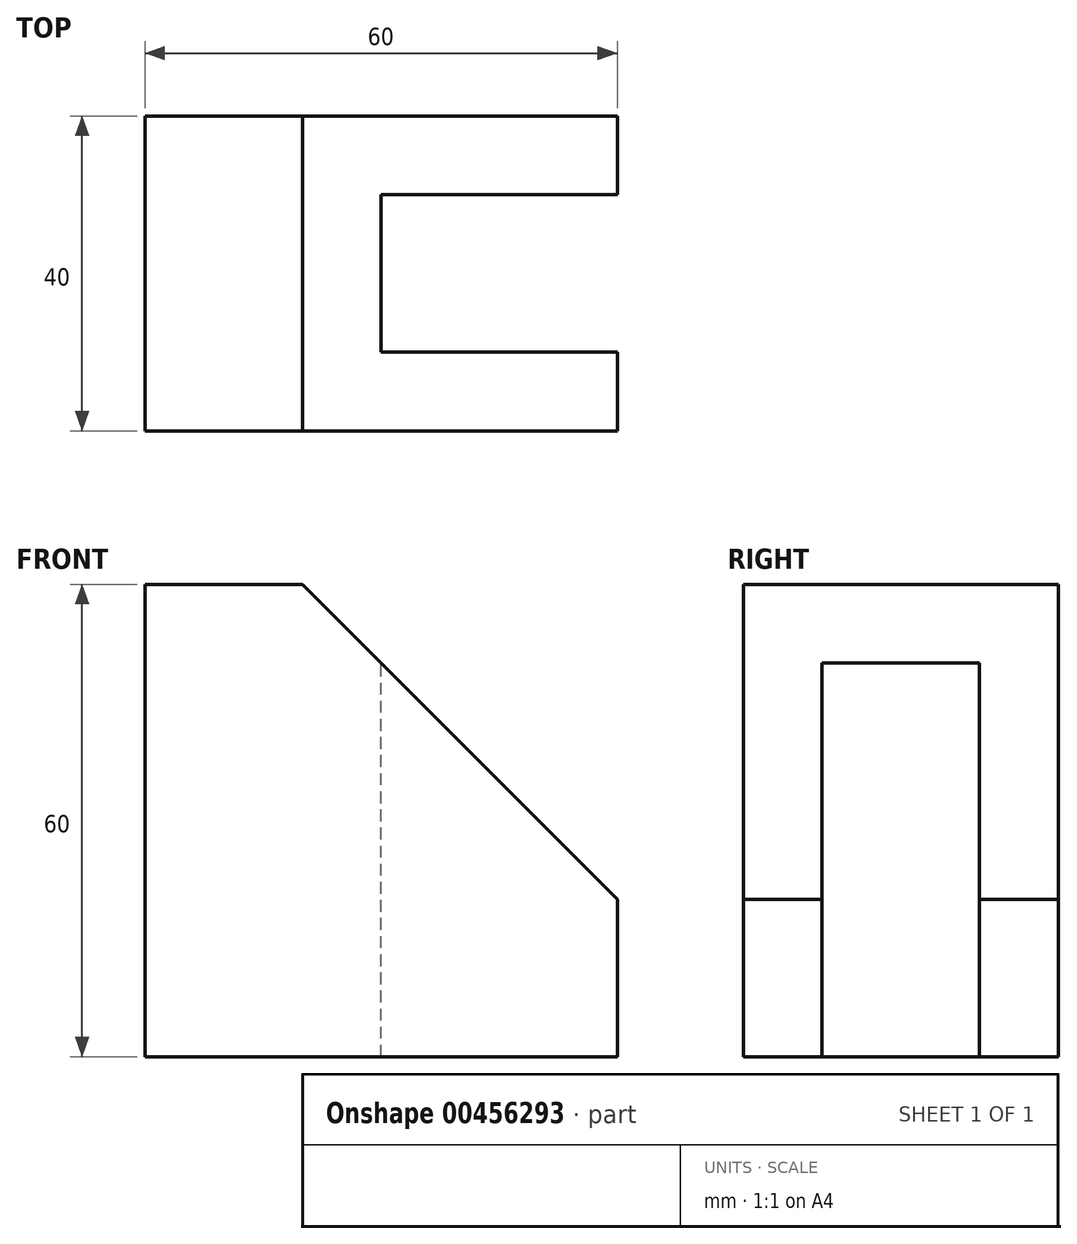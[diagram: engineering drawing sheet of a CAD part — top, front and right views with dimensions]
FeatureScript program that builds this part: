
annotation { "Feature Type Name" : "Feature", "Feature Type Description" : "" }
export const myFeature = defineFeature(function(context is Context, id is Id, definition is map)
    precondition{}
    {
        {
            var Q0;
            Q0=qCreatedBy(makeId("Front.planeOp"),FACE);
            var sketch = newSketch(context, id + "F0", { "sketchPlane" : qUnion([Q0])});
            skLineSegment(sketch, "E0", {"start": v(0, 0) * mm, "end": v(0, 60) * mm});
            skLineSegment(sketch, "E1", {"start": v(0, 60) * mm, "end": v(20, 60) * mm});
            skLineSegment(sketch, "E2", {"start": v(60, 0) * mm, "end": v(0, 0) * mm});
            skLineSegment(sketch, "E3", {"start": v(60, 0) * mm, "end": v(60, 20) * mm});
            skLineSegment(sketch, "E4", {"start": v(20, 60) * mm, "end": v(60, 20) * mm});
            skLineSegment(sketch, "E5", {"start": v(30, 0) * mm, "end": v(30, 50) * mm});
            skSolve(sketch);
        }
        {
            var Q0;
            {var subQ1=sQuery(id+"F0.wireOp",EDGE,"E0");Q0=makeQuery(id+"F0.imprint","IMPRINT",FACE,{"disambiguationData":[TD([[makeQuery(id+"F0.imprint","IMPRINT",EDGE,{"derivedFrom":subQ1}),-1.0]])]});}
            extrude(context, id + "F1", {"entities" : qUnion([Q0]), "endBound" : BoundingType.SYMMETRIC, "depth" : 40 * mm});
        }
        {
            var Q0;
            {var subQ0=sQuery(id+"F0.wireOp",EDGE,"E3");Q0=makeQuery(id+"F0.imprint","IMPRINT",FACE,{"disambiguationData":[TD([[makeQuery(id+"F0.imprint","IMPRINT",EDGE,{"derivedFrom":subQ0}),1.0]])]});}
            extrude(context, id + "F2", {"entities" : qUnion([Q0]), "operationType" : NewBodyOperationType.ADD, "endBound" : BoundingType.SYMMETRIC, "depth" : 40 * mm});
        }
        {
            var Q0;
            {var subQ0=sQuery(id+"F0.wireOp",EDGE,"E3");Q0=makeQuery(id+"F0.imprint","IMPRINT",FACE,{"disambiguationData":[TD([[makeQuery(id+"F0.imprint","IMPRINT",EDGE,{"derivedFrom":subQ0}),1.0]])]});}
            extrude(context, id + "F3", {"entities" : qUnion([Q0]), "operationType" : NewBodyOperationType.REMOVE, "endBound" : BoundingType.SYMMETRIC, "oppositeDirection" : true, "depth" : 20 * mm});
        }
    });
